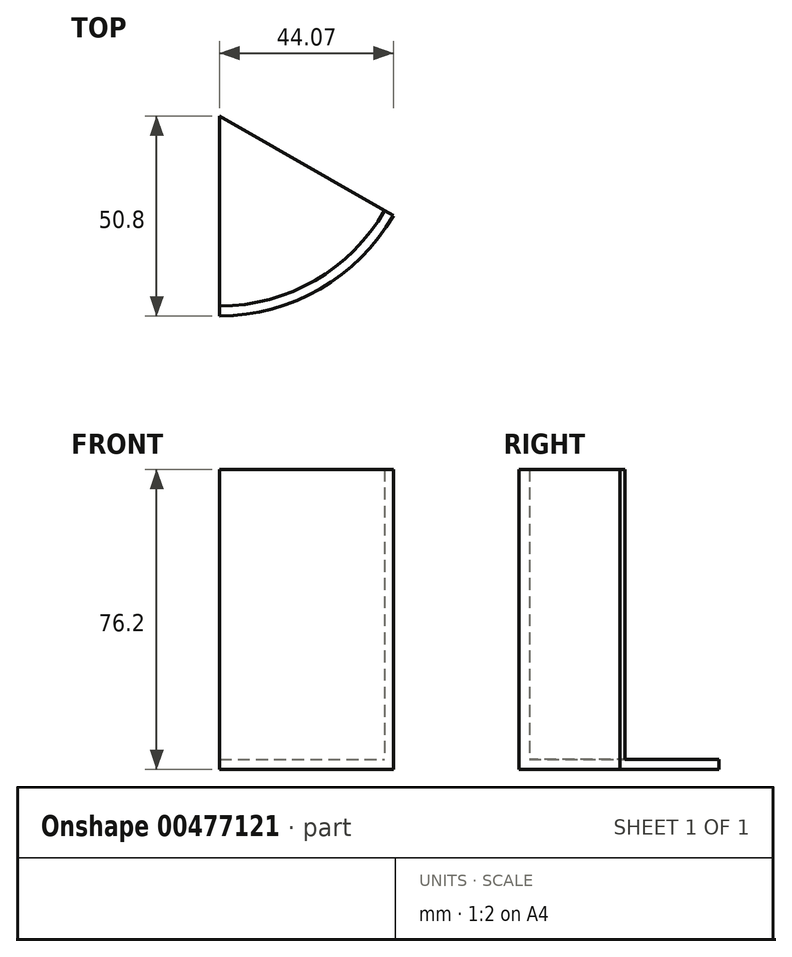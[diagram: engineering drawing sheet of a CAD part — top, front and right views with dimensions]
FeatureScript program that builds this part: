
annotation { "Feature Type Name" : "Feature", "Feature Type Description" : "" }
export const myFeature = defineFeature(function(context is Context, id is Id, definition is map)
    precondition{}
    {
        {
            var Q0;
            Q0=qCreatedBy(makeId("Top.planeOp"),FACE);
            var sketch = newSketch(context, id + "F0", { "sketchPlane" : qUnion([Q0])});
            skCircle(sketch, "E0", {"center": v(0, 0) * mm, "radius": 50.8 * mm});
            skSolve(sketch);
        }
        {
            var Q0;
            Q0=qSketchRegion(id+"F0",true);
            extrude(context, id + "F1", {"entities" : qUnion([Q0]), "depth" : 76.2 * mm});
        }
        {
            var Q0;
            Q0=makeQuery(id+"F1.opExtrude","CAP_FACE",FACE,{"disambiguationData":[OSD([sQuery(id+"F0.wireOp",EDGE,"E0")])],"isStart":false});
            var sketch = newSketch(context, id + "F2", { "sketchPlane" : qUnion([Q0])});
            skLineSegment(sketch, "E1", {"start": v(0, 0) * mm, "end": v(0, -50.8) * mm});
            skLineSegment(sketch, "E2", {"start": v(0, 0) * mm, "end": v(44.07, -25.26) * mm});
            skSolve(sketch);
        }
        {
            var Q0;
            Q0=makeQuery(id+"F1.opExtrude","CAP_FACE",FACE,{"disambiguationData":[OSD([sQuery(id+"F0.wireOp",EDGE,"E0")])],"isStart":false});
            shell(context, id + "F3", {"entities" : qUnion([Q0]), "thickness" : 2.54 * mm});
        }
        {
            var Q0;
            {var subQ0=sQuery(id+"F2.wireOp",EDGE,"E1");Q0=makeQuery(id+"F2.imprint","IMPRINT",FACE,{"disambiguationData":[TD([[makeQuery(id+"F2.imprint","IMPRINT",EDGE,{"derivedFrom":subQ0}),-1.0]])]});}
            extrude(context, id + "F4", {"entities" : qUnion([Q0]), "operationType" : NewBodyOperationType.REMOVE, "oppositeDirection" : true, "depth" : 76.2 * mm});
        }
    });
